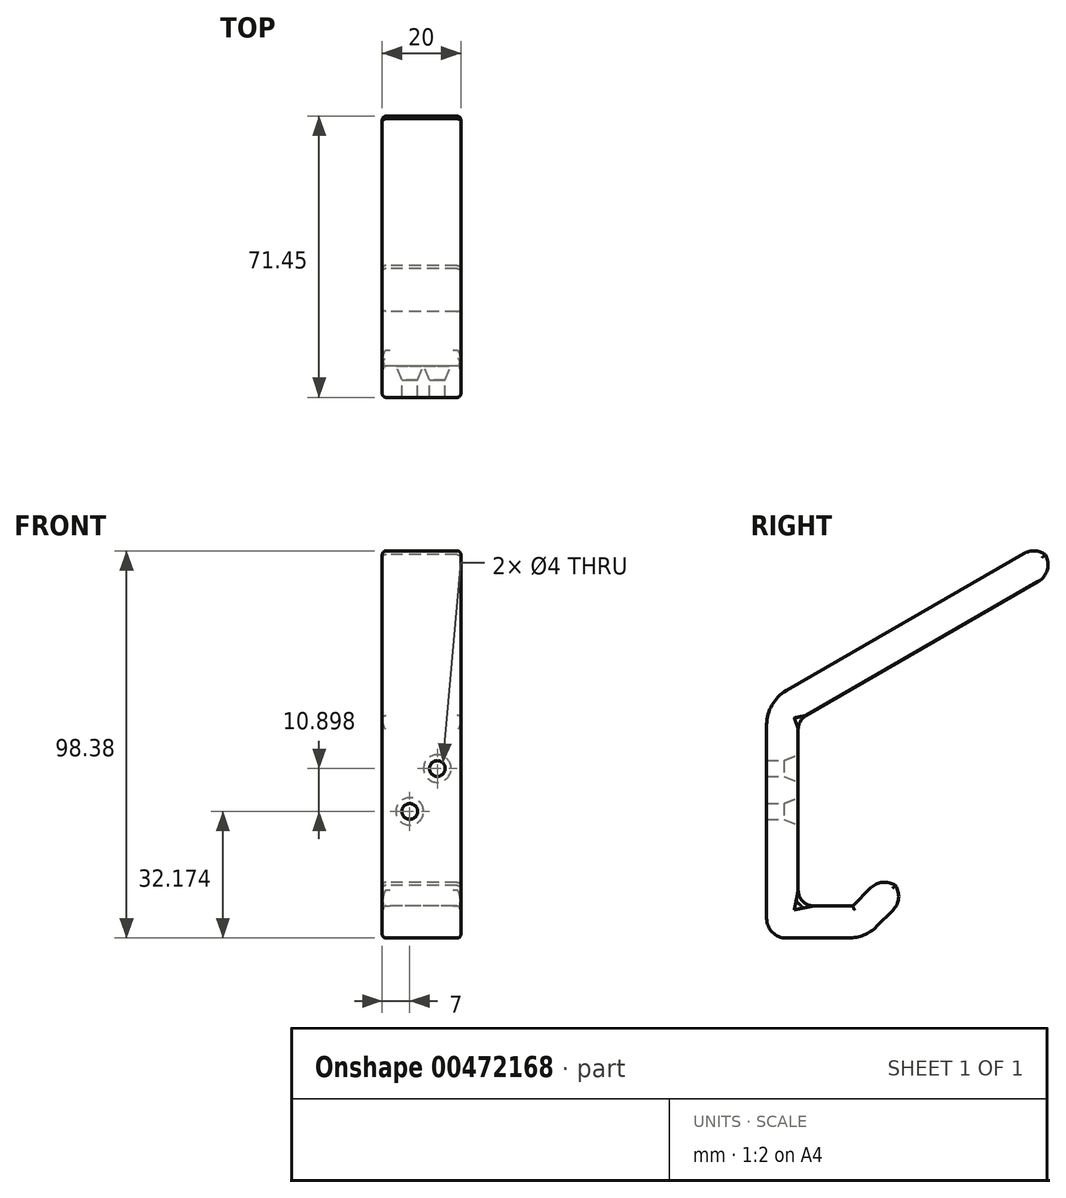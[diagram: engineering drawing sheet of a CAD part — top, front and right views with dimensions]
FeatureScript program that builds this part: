
annotation { "Feature Type Name" : "Feature", "Feature Type Description" : "" }
export const myFeature = defineFeature(function(context is Context, id is Id, definition is map)
    precondition{}
    {
        {
            var Q0;
            Q0=qCreatedBy(makeId("Right.planeOp"),FACE);
            var sketch = newSketch(context, id + "F0", { "sketchPlane" : qUnion([Q0])});
            skLineSegment(sketch, "E0", {"start": v(-17.53, 60) * mm, "end": v(51.75, 100) * mm});
            skLineSegment(sketch, "E1", {"start": v(7.47, 0) * mm, "end": v(18.07, 10.6) * mm});
            skLineSegment(sketch, "E2", {"start": v(51.75, 100) * mm, "end": v(55.75, 93.07) * mm});
            skLineSegment(sketch, "E3", {"start": v(55.75, 93.07) * mm, "end": v(-9.53, 55.38) * mm});
            skLineSegment(sketch, "E4", {"start": v(-9.53, 55.38) * mm, "end": v(-9.53, 8) * mm});
            skLineSegment(sketch, "E5", {"start": v(-9.71, 8.17) * mm, "end": v(4.33, 8.17) * mm});
            skLineSegment(sketch, "E6", {"start": v(18.07, 10.6) * mm, "end": v(12.42, 16.26) * mm});
            skLineSegment(sketch, "E7", {"start": v(12.42, 16.26) * mm, "end": v(4.33, 8.17) * mm});
            skLineSegment(sketch, "E8", {"start": v(-17.53, 60) * mm, "end": v(-17.53, 0) * mm});
            skLineSegment(sketch, "E9", {"start": v(7.47, 0) * mm, "end": v(-17.53, 0) * mm});
            skSolve(sketch);
        }
        {
            var Q0;
            Q0=makeQuery(id+"F0.imprint","IMPRINT",FACE,{"disambiguationData":[TD([[makeQuery(id+"F0.imprint","IMPRINT",EDGE,{"derivedFrom":sQuery(id+"F0.wireOp",EDGE,"E0")}),-1.0]])]});
            extrude(context, id + "F1", {"entities" : qUnion([Q0]), "depth" : 20 * mm});
        }
        {
            var Q0;
            Q0=makeQuery(id+"F1.opExtrude","SWEPT_EDGE",EDGE,{"disambiguationData":[OSD([sQuery(id+"F0.wireOp",EDGE,"E2"),sQuery(id+"F0.wireOp",EDGE,"E3")])]});
            fillet(context, id + "F2", {"entities" : qUnion([Q0]), "radius" : 5 * mm, "tangentPropagation" : true, "allowEdgeOverflow" : false});
        }
        {
            var Q0;
            Q0=makeQuery(id+"F1.opExtrude","SWEPT_EDGE",EDGE,{"disambiguationData":[OSD([sQuery(id+"F0.wireOp",EDGE,"E0"),sQuery(id+"F0.wireOp",EDGE,"E2")])]});
            fillet(context, id + "F3", {"entities" : qUnion([Q0]), "radius" : 5 * mm, "tangentPropagation" : true, "allowEdgeOverflow" : false});
        }
        {
            var Q0;
            Q0=makeQuery(id+"F1.opExtrude","SWEPT_EDGE",EDGE,{"disambiguationData":[OSD([sQuery(id+"F0.wireOp",EDGE,"E0"),sQuery(id+"F0.wireOp",EDGE,"E8")])]});
            fillet(context, id + "F4", {"entities" : qUnion([Q0]), "radius" : 10 * mm, "tangentPropagation" : true, "allowEdgeOverflow" : false});
        }
        {
            var Q0;
            Q0=makeQuery(id+"F1.opExtrude","SWEPT_EDGE",EDGE,{"disambiguationData":[OSD([sQuery(id+"F0.wireOp",EDGE,"E8"),sQuery(id+"F0.wireOp",EDGE,"E9")])]});
            fillet(context, id + "F5", {"entities" : qUnion([Q0]), "radius" : 5 * mm, "tangentPropagation" : true, "allowEdgeOverflow" : false});
        }
        {
            var Q0;
            Q0=makeQuery(id+"F1.opExtrude","SWEPT_EDGE",EDGE,{"disambiguationData":[OSD([sQuery(id+"F0.wireOp",EDGE,"E1"),sQuery(id+"F0.wireOp",EDGE,"E9")])]});
            fillet(context, id + "F6", {"entities" : qUnion([Q0]), "radius" : 10 * mm, "tangentPropagation" : true, "allowEdgeOverflow" : false});
        }
        {
            var Q0;
            Q0=makeQuery(id+"F1.opExtrude","SWEPT_EDGE",EDGE,{"disambiguationData":[OSD([sQuery(id+"F0.wireOp",EDGE,"E1"),sQuery(id+"F0.wireOp",EDGE,"E6")])]});
            var Q1;
            Q1=makeQuery(id+"F1.opExtrude","SWEPT_EDGE",EDGE,{"disambiguationData":[OSD([sQuery(id+"F0.wireOp",EDGE,"E6"),sQuery(id+"F0.wireOp",EDGE,"E7")])]});
            fillet(context, id + "F7", {"entities" : qUnion([Q0, Q1]), "radius" : 5 * mm, "tangentPropagation" : true, "allowEdgeOverflow" : false});
        }
        {
            var Q0;
            {var subQ0=sQuery(id+"F0.wireOp",EDGE,"E7");var subQ1=sQuery(id+"F0.wireOp",EDGE,"E6");Q0=makeQuery(id+"F7.opFillet","BLEND_EDGE",EDGE,{"blendedFrom":[makeQuery(id+"F1.opExtrude","SWEPT_EDGE",EDGE,{"disambiguationData":[OSD([subQ1,subQ0])]}),makeQuery(id+"F1.opExtrude","CAP_FACE",FACE,{"disambiguationData":[OSD([sQuery(id+"F0.wireOp",EDGE,"E0"),sQuery(id+"F0.wireOp",EDGE,"E1"),sQuery(id+"F0.wireOp",EDGE,"E2"),sQuery(id+"F0.wireOp",EDGE,"E3"),sQuery(id+"F0.wireOp",EDGE,"E4"),sQuery(id+"F0.wireOp",EDGE,"E5"),subQ1,subQ0,sQuery(id+"F0.wireOp",EDGE,"E8"),sQuery(id+"F0.wireOp",EDGE,"E9")])],"isStart":true})],"blendedInto":[makeQuery(id+"F1.opExtrude","CAP_FACE",FACE,{"disambiguationData":[OSD([sQuery(id+"F0.wireOp",EDGE,"E0"),sQuery(id+"F0.wireOp",EDGE,"E1"),sQuery(id+"F0.wireOp",EDGE,"E2"),sQuery(id+"F0.wireOp",EDGE,"E3"),sQuery(id+"F0.wireOp",EDGE,"E4"),sQuery(id+"F0.wireOp",EDGE,"E5"),subQ1,subQ0,sQuery(id+"F0.wireOp",EDGE,"E8"),sQuery(id+"F0.wireOp",EDGE,"E9")])],"isStart":true})]});}
            var Q1;
            {var subQ0=sQuery(id+"F0.wireOp",EDGE,"E6");var subQ1=sQuery(id+"F0.wireOp",EDGE,"E1");Q1=makeQuery(id+"F7.opFillet","BLEND_EDGE",EDGE,{"blendedFrom":[makeQuery(id+"F1.opExtrude","SWEPT_EDGE",EDGE,{"disambiguationData":[OSD([subQ1,subQ0])]}),makeQuery(id+"F1.opExtrude","CAP_FACE",FACE,{"disambiguationData":[OSD([sQuery(id+"F0.wireOp",EDGE,"E0"),subQ1,sQuery(id+"F0.wireOp",EDGE,"E2"),sQuery(id+"F0.wireOp",EDGE,"E3"),sQuery(id+"F0.wireOp",EDGE,"E4"),sQuery(id+"F0.wireOp",EDGE,"E5"),subQ0,sQuery(id+"F0.wireOp",EDGE,"E7"),sQuery(id+"F0.wireOp",EDGE,"E8"),sQuery(id+"F0.wireOp",EDGE,"E9")])],"isStart":true})],"blendedInto":[makeQuery(id+"F1.opExtrude","CAP_FACE",FACE,{"disambiguationData":[OSD([sQuery(id+"F0.wireOp",EDGE,"E0"),subQ1,sQuery(id+"F0.wireOp",EDGE,"E2"),sQuery(id+"F0.wireOp",EDGE,"E3"),sQuery(id+"F0.wireOp",EDGE,"E4"),sQuery(id+"F0.wireOp",EDGE,"E5"),subQ0,sQuery(id+"F0.wireOp",EDGE,"E7"),sQuery(id+"F0.wireOp",EDGE,"E8"),sQuery(id+"F0.wireOp",EDGE,"E9")])],"isStart":true})]});}
            var Q2;
            Q2=makeQuery(id+"F1.opExtrude","CAP_EDGE",EDGE,{"disambiguationData":[OSD([sQuery(id+"F0.wireOp",EDGE,"E7")])],"isStart":true});
            var Q3;
            Q3=makeQuery(id+"F1.opExtrude","CAP_EDGE",EDGE,{"disambiguationData":[OSD([sQuery(id+"F0.wireOp",EDGE,"E5")])],"isStart":true});
            var Q4;
            {var subQ0=sQuery(id+"F0.wireOp",EDGE,"E9");var subQ1=sQuery(id+"F0.wireOp",EDGE,"E1");Q4=makeQuery(id+"F6.opFillet","BLEND_EDGE",EDGE,{"blendedFrom":[makeQuery(id+"F1.opExtrude","SWEPT_EDGE",EDGE,{"disambiguationData":[OSD([subQ1,subQ0])]}),makeQuery(id+"F1.opExtrude","CAP_FACE",FACE,{"disambiguationData":[OSD([sQuery(id+"F0.wireOp",EDGE,"E0"),subQ1,sQuery(id+"F0.wireOp",EDGE,"E2"),sQuery(id+"F0.wireOp",EDGE,"E3"),sQuery(id+"F0.wireOp",EDGE,"E4"),sQuery(id+"F0.wireOp",EDGE,"E5"),sQuery(id+"F0.wireOp",EDGE,"E6"),sQuery(id+"F0.wireOp",EDGE,"E7"),sQuery(id+"F0.wireOp",EDGE,"E8"),subQ0])],"isStart":true})],"blendedInto":[makeQuery(id+"F1.opExtrude","CAP_FACE",FACE,{"disambiguationData":[OSD([sQuery(id+"F0.wireOp",EDGE,"E0"),subQ1,sQuery(id+"F0.wireOp",EDGE,"E2"),sQuery(id+"F0.wireOp",EDGE,"E3"),sQuery(id+"F0.wireOp",EDGE,"E4"),sQuery(id+"F0.wireOp",EDGE,"E5"),sQuery(id+"F0.wireOp",EDGE,"E6"),sQuery(id+"F0.wireOp",EDGE,"E7"),sQuery(id+"F0.wireOp",EDGE,"E8"),subQ0])],"isStart":true})]});}
            var Q5;
            Q5=makeQuery(id+"F1.opExtrude","CAP_EDGE",EDGE,{"disambiguationData":[OSD([sQuery(id+"F0.wireOp",EDGE,"E1")])],"isStart":true});
            var Q6;
            Q6=makeQuery(id+"F1.opExtrude","CAP_EDGE",EDGE,{"disambiguationData":[OSD([sQuery(id+"F0.wireOp",EDGE,"E9")])],"isStart":true});
            var Q7;
            {var subQ0=sQuery(id+"F0.wireOp",EDGE,"E9");var subQ1=sQuery(id+"F0.wireOp",EDGE,"E8");Q7=makeQuery(id+"F5.opFillet","BLEND_EDGE",EDGE,{"blendedFrom":[makeQuery(id+"F1.opExtrude","SWEPT_EDGE",EDGE,{"disambiguationData":[OSD([subQ1,subQ0])]}),makeQuery(id+"F1.opExtrude","CAP_FACE",FACE,{"disambiguationData":[OSD([sQuery(id+"F0.wireOp",EDGE,"E0"),sQuery(id+"F0.wireOp",EDGE,"E1"),sQuery(id+"F0.wireOp",EDGE,"E2"),sQuery(id+"F0.wireOp",EDGE,"E3"),sQuery(id+"F0.wireOp",EDGE,"E4"),sQuery(id+"F0.wireOp",EDGE,"E5"),sQuery(id+"F0.wireOp",EDGE,"E6"),sQuery(id+"F0.wireOp",EDGE,"E7"),subQ1,subQ0])],"isStart":true})],"blendedInto":[makeQuery(id+"F1.opExtrude","CAP_FACE",FACE,{"disambiguationData":[OSD([sQuery(id+"F0.wireOp",EDGE,"E0"),sQuery(id+"F0.wireOp",EDGE,"E1"),sQuery(id+"F0.wireOp",EDGE,"E2"),sQuery(id+"F0.wireOp",EDGE,"E3"),sQuery(id+"F0.wireOp",EDGE,"E4"),sQuery(id+"F0.wireOp",EDGE,"E5"),sQuery(id+"F0.wireOp",EDGE,"E6"),sQuery(id+"F0.wireOp",EDGE,"E7"),subQ1,subQ0])],"isStart":true})]});}
            var Q8;
            Q8=makeQuery(id+"F1.opExtrude","CAP_EDGE",EDGE,{"disambiguationData":[OSD([sQuery(id+"F0.wireOp",EDGE,"E8")])],"isStart":true});
            var Q9;
            Q9=makeQuery(id+"F1.opExtrude","CAP_EDGE",EDGE,{"disambiguationData":[OSD([sQuery(id+"F0.wireOp",EDGE,"E4")])],"isStart":true});
            var Q10;
            Q10=makeQuery(id+"F1.opExtrude","CAP_EDGE",EDGE,{"disambiguationData":[OSD([sQuery(id+"F0.wireOp",EDGE,"E3")])],"isStart":true});
            var Q11;
            Q11=makeQuery(id+"F1.opExtrude","CAP_EDGE",EDGE,{"disambiguationData":[OSD([sQuery(id+"F0.wireOp",EDGE,"E0")])],"isStart":true});
            var Q12;
            {var subQ0=sQuery(id+"F0.wireOp",EDGE,"E2");var subQ1=sQuery(id+"F0.wireOp",EDGE,"E0");Q12=makeQuery(id+"F3.opFillet","BLEND_EDGE",EDGE,{"blendedFrom":[makeQuery(id+"F1.opExtrude","SWEPT_EDGE",EDGE,{"disambiguationData":[OSD([subQ1,subQ0])]}),makeQuery(id+"F1.opExtrude","CAP_FACE",FACE,{"disambiguationData":[OSD([subQ1,sQuery(id+"F0.wireOp",EDGE,"E1"),subQ0,sQuery(id+"F0.wireOp",EDGE,"E3"),sQuery(id+"F0.wireOp",EDGE,"E4"),sQuery(id+"F0.wireOp",EDGE,"E5"),sQuery(id+"F0.wireOp",EDGE,"E6"),sQuery(id+"F0.wireOp",EDGE,"E7"),sQuery(id+"F0.wireOp",EDGE,"E8"),sQuery(id+"F0.wireOp",EDGE,"E9")])],"isStart":true})],"blendedInto":[makeQuery(id+"F1.opExtrude","CAP_FACE",FACE,{"disambiguationData":[OSD([subQ1,sQuery(id+"F0.wireOp",EDGE,"E1"),subQ0,sQuery(id+"F0.wireOp",EDGE,"E3"),sQuery(id+"F0.wireOp",EDGE,"E4"),sQuery(id+"F0.wireOp",EDGE,"E5"),sQuery(id+"F0.wireOp",EDGE,"E6"),sQuery(id+"F0.wireOp",EDGE,"E7"),sQuery(id+"F0.wireOp",EDGE,"E8"),sQuery(id+"F0.wireOp",EDGE,"E9")])],"isStart":true})]});}
            var Q13;
            {var subQ0=sQuery(id+"F0.wireOp",EDGE,"E3");var subQ1=sQuery(id+"F0.wireOp",EDGE,"E2");Q13=makeQuery(id+"F2.opFillet","BLEND_EDGE",EDGE,{"blendedFrom":[makeQuery(id+"F1.opExtrude","SWEPT_EDGE",EDGE,{"disambiguationData":[OSD([subQ1,subQ0])]}),makeQuery(id+"F1.opExtrude","CAP_FACE",FACE,{"disambiguationData":[OSD([sQuery(id+"F0.wireOp",EDGE,"E0"),sQuery(id+"F0.wireOp",EDGE,"E1"),subQ1,subQ0,sQuery(id+"F0.wireOp",EDGE,"E4"),sQuery(id+"F0.wireOp",EDGE,"E5"),sQuery(id+"F0.wireOp",EDGE,"E6"),sQuery(id+"F0.wireOp",EDGE,"E7"),sQuery(id+"F0.wireOp",EDGE,"E8"),sQuery(id+"F0.wireOp",EDGE,"E9")])],"isStart":true})],"blendedInto":[makeQuery(id+"F1.opExtrude","CAP_FACE",FACE,{"disambiguationData":[OSD([sQuery(id+"F0.wireOp",EDGE,"E0"),sQuery(id+"F0.wireOp",EDGE,"E1"),subQ1,subQ0,sQuery(id+"F0.wireOp",EDGE,"E4"),sQuery(id+"F0.wireOp",EDGE,"E5"),sQuery(id+"F0.wireOp",EDGE,"E6"),sQuery(id+"F0.wireOp",EDGE,"E7"),sQuery(id+"F0.wireOp",EDGE,"E8"),sQuery(id+"F0.wireOp",EDGE,"E9")])],"isStart":true})]});}
            var Q14;
            {var subQ0=sQuery(id+"F0.wireOp",EDGE,"E8");var subQ1=sQuery(id+"F0.wireOp",EDGE,"E0");Q14=makeQuery(id+"F4.opFillet","BLEND_EDGE",EDGE,{"blendedFrom":[makeQuery(id+"F1.opExtrude","SWEPT_EDGE",EDGE,{"disambiguationData":[OSD([subQ1,subQ0])]}),makeQuery(id+"F1.opExtrude","CAP_FACE",FACE,{"disambiguationData":[OSD([subQ1,sQuery(id+"F0.wireOp",EDGE,"E1"),sQuery(id+"F0.wireOp",EDGE,"E2"),sQuery(id+"F0.wireOp",EDGE,"E3"),sQuery(id+"F0.wireOp",EDGE,"E4"),sQuery(id+"F0.wireOp",EDGE,"E5"),sQuery(id+"F0.wireOp",EDGE,"E6"),sQuery(id+"F0.wireOp",EDGE,"E7"),subQ0,sQuery(id+"F0.wireOp",EDGE,"E9")])],"isStart":true})],"blendedInto":[makeQuery(id+"F1.opExtrude","CAP_FACE",FACE,{"disambiguationData":[OSD([subQ1,sQuery(id+"F0.wireOp",EDGE,"E1"),sQuery(id+"F0.wireOp",EDGE,"E2"),sQuery(id+"F0.wireOp",EDGE,"E3"),sQuery(id+"F0.wireOp",EDGE,"E4"),sQuery(id+"F0.wireOp",EDGE,"E5"),sQuery(id+"F0.wireOp",EDGE,"E6"),sQuery(id+"F0.wireOp",EDGE,"E7"),subQ0,sQuery(id+"F0.wireOp",EDGE,"E9")])],"isStart":true})]});}
            var Q15;
            Q15=makeQuery(id+"F1.opExtrude","CAP_EDGE",EDGE,{"disambiguationData":[OSD([sQuery(id+"F0.wireOp",EDGE,"E0")])],"isStart":false});
            var Q16;
            Q16=makeQuery(id+"F1.opExtrude","CAP_EDGE",EDGE,{"disambiguationData":[OSD([sQuery(id+"F0.wireOp",EDGE,"E3")])],"isStart":false});
            var Q17;
            {var subQ0=sQuery(id+"F0.wireOp",EDGE,"E8");var subQ1=sQuery(id+"F0.wireOp",EDGE,"E0");Q17=makeQuery(id+"F4.opFillet","BLEND_EDGE",EDGE,{"blendedFrom":[makeQuery(id+"F1.opExtrude","SWEPT_EDGE",EDGE,{"disambiguationData":[OSD([subQ1,subQ0])]}),makeQuery(id+"F1.opExtrude","CAP_FACE",FACE,{"disambiguationData":[OSD([subQ1,sQuery(id+"F0.wireOp",EDGE,"E1"),sQuery(id+"F0.wireOp",EDGE,"E2"),sQuery(id+"F0.wireOp",EDGE,"E3"),sQuery(id+"F0.wireOp",EDGE,"E4"),sQuery(id+"F0.wireOp",EDGE,"E5"),sQuery(id+"F0.wireOp",EDGE,"E6"),sQuery(id+"F0.wireOp",EDGE,"E7"),subQ0,sQuery(id+"F0.wireOp",EDGE,"E9")])],"isStart":false})],"blendedInto":[makeQuery(id+"F1.opExtrude","CAP_FACE",FACE,{"disambiguationData":[OSD([subQ1,sQuery(id+"F0.wireOp",EDGE,"E1"),sQuery(id+"F0.wireOp",EDGE,"E2"),sQuery(id+"F0.wireOp",EDGE,"E3"),sQuery(id+"F0.wireOp",EDGE,"E4"),sQuery(id+"F0.wireOp",EDGE,"E5"),sQuery(id+"F0.wireOp",EDGE,"E6"),sQuery(id+"F0.wireOp",EDGE,"E7"),subQ0,sQuery(id+"F0.wireOp",EDGE,"E9")])],"isStart":false})]});}
            var Q18;
            {var subQ0=sQuery(id+"F0.wireOp",EDGE,"E2");var subQ1=sQuery(id+"F0.wireOp",EDGE,"E0");Q18=makeQuery(id+"F3.opFillet","BLEND_EDGE",EDGE,{"blendedFrom":[makeQuery(id+"F1.opExtrude","SWEPT_EDGE",EDGE,{"disambiguationData":[OSD([subQ1,subQ0])]}),makeQuery(id+"F1.opExtrude","CAP_FACE",FACE,{"disambiguationData":[OSD([subQ1,sQuery(id+"F0.wireOp",EDGE,"E1"),subQ0,sQuery(id+"F0.wireOp",EDGE,"E3"),sQuery(id+"F0.wireOp",EDGE,"E4"),sQuery(id+"F0.wireOp",EDGE,"E5"),sQuery(id+"F0.wireOp",EDGE,"E6"),sQuery(id+"F0.wireOp",EDGE,"E7"),sQuery(id+"F0.wireOp",EDGE,"E8"),sQuery(id+"F0.wireOp",EDGE,"E9")])],"isStart":false})],"blendedInto":[makeQuery(id+"F1.opExtrude","CAP_FACE",FACE,{"disambiguationData":[OSD([subQ1,sQuery(id+"F0.wireOp",EDGE,"E1"),subQ0,sQuery(id+"F0.wireOp",EDGE,"E3"),sQuery(id+"F0.wireOp",EDGE,"E4"),sQuery(id+"F0.wireOp",EDGE,"E5"),sQuery(id+"F0.wireOp",EDGE,"E6"),sQuery(id+"F0.wireOp",EDGE,"E7"),sQuery(id+"F0.wireOp",EDGE,"E8"),sQuery(id+"F0.wireOp",EDGE,"E9")])],"isStart":false})]});}
            var Q19;
            {var subQ0=sQuery(id+"F0.wireOp",EDGE,"E3");var subQ1=sQuery(id+"F0.wireOp",EDGE,"E2");Q19=makeQuery(id+"F2.opFillet","BLEND_EDGE",EDGE,{"blendedFrom":[makeQuery(id+"F1.opExtrude","SWEPT_EDGE",EDGE,{"disambiguationData":[OSD([subQ1,subQ0])]}),makeQuery(id+"F1.opExtrude","CAP_FACE",FACE,{"disambiguationData":[OSD([sQuery(id+"F0.wireOp",EDGE,"E0"),sQuery(id+"F0.wireOp",EDGE,"E1"),subQ1,subQ0,sQuery(id+"F0.wireOp",EDGE,"E4"),sQuery(id+"F0.wireOp",EDGE,"E5"),sQuery(id+"F0.wireOp",EDGE,"E6"),sQuery(id+"F0.wireOp",EDGE,"E7"),sQuery(id+"F0.wireOp",EDGE,"E8"),sQuery(id+"F0.wireOp",EDGE,"E9")])],"isStart":false})],"blendedInto":[makeQuery(id+"F1.opExtrude","CAP_FACE",FACE,{"disambiguationData":[OSD([sQuery(id+"F0.wireOp",EDGE,"E0"),sQuery(id+"F0.wireOp",EDGE,"E1"),subQ1,subQ0,sQuery(id+"F0.wireOp",EDGE,"E4"),sQuery(id+"F0.wireOp",EDGE,"E5"),sQuery(id+"F0.wireOp",EDGE,"E6"),sQuery(id+"F0.wireOp",EDGE,"E7"),sQuery(id+"F0.wireOp",EDGE,"E8"),sQuery(id+"F0.wireOp",EDGE,"E9")])],"isStart":false})]});}
            var Q20;
            Q20=makeQuery(id+"F1.opExtrude","CAP_EDGE",EDGE,{"disambiguationData":[OSD([sQuery(id+"F0.wireOp",EDGE,"E4")])],"isStart":false});
            var Q21;
            Q21=makeQuery(id+"F1.opExtrude","CAP_EDGE",EDGE,{"disambiguationData":[OSD([sQuery(id+"F0.wireOp",EDGE,"E8")])],"isStart":false});
            var Q22;
            {var subQ0=sQuery(id+"F0.wireOp",EDGE,"E9");var subQ1=sQuery(id+"F0.wireOp",EDGE,"E8");Q22=makeQuery(id+"F5.opFillet","BLEND_EDGE",EDGE,{"blendedFrom":[makeQuery(id+"F1.opExtrude","SWEPT_EDGE",EDGE,{"disambiguationData":[OSD([subQ1,subQ0])]}),makeQuery(id+"F1.opExtrude","CAP_FACE",FACE,{"disambiguationData":[OSD([sQuery(id+"F0.wireOp",EDGE,"E0"),sQuery(id+"F0.wireOp",EDGE,"E1"),sQuery(id+"F0.wireOp",EDGE,"E2"),sQuery(id+"F0.wireOp",EDGE,"E3"),sQuery(id+"F0.wireOp",EDGE,"E4"),sQuery(id+"F0.wireOp",EDGE,"E5"),sQuery(id+"F0.wireOp",EDGE,"E6"),sQuery(id+"F0.wireOp",EDGE,"E7"),subQ1,subQ0])],"isStart":false})],"blendedInto":[makeQuery(id+"F1.opExtrude","CAP_FACE",FACE,{"disambiguationData":[OSD([sQuery(id+"F0.wireOp",EDGE,"E0"),sQuery(id+"F0.wireOp",EDGE,"E1"),sQuery(id+"F0.wireOp",EDGE,"E2"),sQuery(id+"F0.wireOp",EDGE,"E3"),sQuery(id+"F0.wireOp",EDGE,"E4"),sQuery(id+"F0.wireOp",EDGE,"E5"),sQuery(id+"F0.wireOp",EDGE,"E6"),sQuery(id+"F0.wireOp",EDGE,"E7"),subQ1,subQ0])],"isStart":false})]});}
            var Q23;
            Q23=makeQuery(id+"F1.opExtrude","CAP_EDGE",EDGE,{"disambiguationData":[OSD([sQuery(id+"F0.wireOp",EDGE,"E9")])],"isStart":false});
            var Q24;
            Q24=makeQuery(id+"F1.opExtrude","CAP_EDGE",EDGE,{"disambiguationData":[OSD([sQuery(id+"F0.wireOp",EDGE,"E5")])],"isStart":false});
            var Q25;
            Q25=makeQuery(id+"F1.opExtrude","CAP_EDGE",EDGE,{"disambiguationData":[OSD([sQuery(id+"F0.wireOp",EDGE,"E7")])],"isStart":false});
            var Q26;
            {var subQ0=sQuery(id+"F0.wireOp",EDGE,"E7");var subQ1=sQuery(id+"F0.wireOp",EDGE,"E6");Q26=makeQuery(id+"F7.opFillet","BLEND_EDGE",EDGE,{"blendedFrom":[makeQuery(id+"F1.opExtrude","SWEPT_EDGE",EDGE,{"disambiguationData":[OSD([subQ1,subQ0])]}),makeQuery(id+"F1.opExtrude","CAP_FACE",FACE,{"disambiguationData":[OSD([sQuery(id+"F0.wireOp",EDGE,"E0"),sQuery(id+"F0.wireOp",EDGE,"E1"),sQuery(id+"F0.wireOp",EDGE,"E2"),sQuery(id+"F0.wireOp",EDGE,"E3"),sQuery(id+"F0.wireOp",EDGE,"E4"),sQuery(id+"F0.wireOp",EDGE,"E5"),subQ1,subQ0,sQuery(id+"F0.wireOp",EDGE,"E8"),sQuery(id+"F0.wireOp",EDGE,"E9")])],"isStart":false})],"blendedInto":[makeQuery(id+"F1.opExtrude","CAP_FACE",FACE,{"disambiguationData":[OSD([sQuery(id+"F0.wireOp",EDGE,"E0"),sQuery(id+"F0.wireOp",EDGE,"E1"),sQuery(id+"F0.wireOp",EDGE,"E2"),sQuery(id+"F0.wireOp",EDGE,"E3"),sQuery(id+"F0.wireOp",EDGE,"E4"),sQuery(id+"F0.wireOp",EDGE,"E5"),subQ1,subQ0,sQuery(id+"F0.wireOp",EDGE,"E8"),sQuery(id+"F0.wireOp",EDGE,"E9")])],"isStart":false})]});}
            var Q27;
            {var subQ0=sQuery(id+"F0.wireOp",EDGE,"E9");var subQ1=sQuery(id+"F0.wireOp",EDGE,"E1");Q27=makeQuery(id+"F6.opFillet","BLEND_EDGE",EDGE,{"blendedFrom":[makeQuery(id+"F1.opExtrude","SWEPT_EDGE",EDGE,{"disambiguationData":[OSD([subQ1,subQ0])]}),makeQuery(id+"F1.opExtrude","CAP_FACE",FACE,{"disambiguationData":[OSD([sQuery(id+"F0.wireOp",EDGE,"E0"),subQ1,sQuery(id+"F0.wireOp",EDGE,"E2"),sQuery(id+"F0.wireOp",EDGE,"E3"),sQuery(id+"F0.wireOp",EDGE,"E4"),sQuery(id+"F0.wireOp",EDGE,"E5"),sQuery(id+"F0.wireOp",EDGE,"E6"),sQuery(id+"F0.wireOp",EDGE,"E7"),sQuery(id+"F0.wireOp",EDGE,"E8"),subQ0])],"isStart":false})],"blendedInto":[makeQuery(id+"F1.opExtrude","CAP_FACE",FACE,{"disambiguationData":[OSD([sQuery(id+"F0.wireOp",EDGE,"E0"),subQ1,sQuery(id+"F0.wireOp",EDGE,"E2"),sQuery(id+"F0.wireOp",EDGE,"E3"),sQuery(id+"F0.wireOp",EDGE,"E4"),sQuery(id+"F0.wireOp",EDGE,"E5"),sQuery(id+"F0.wireOp",EDGE,"E6"),sQuery(id+"F0.wireOp",EDGE,"E7"),sQuery(id+"F0.wireOp",EDGE,"E8"),subQ0])],"isStart":false})]});}
            var Q28;
            {var subQ0=sQuery(id+"F0.wireOp",EDGE,"E6");var subQ1=sQuery(id+"F0.wireOp",EDGE,"E1");Q28=makeQuery(id+"F7.opFillet","BLEND_EDGE",EDGE,{"blendedFrom":[makeQuery(id+"F1.opExtrude","SWEPT_EDGE",EDGE,{"disambiguationData":[OSD([subQ1,subQ0])]}),makeQuery(id+"F1.opExtrude","CAP_FACE",FACE,{"disambiguationData":[OSD([sQuery(id+"F0.wireOp",EDGE,"E0"),subQ1,sQuery(id+"F0.wireOp",EDGE,"E2"),sQuery(id+"F0.wireOp",EDGE,"E3"),sQuery(id+"F0.wireOp",EDGE,"E4"),sQuery(id+"F0.wireOp",EDGE,"E5"),subQ0,sQuery(id+"F0.wireOp",EDGE,"E7"),sQuery(id+"F0.wireOp",EDGE,"E8"),sQuery(id+"F0.wireOp",EDGE,"E9")])],"isStart":false})],"blendedInto":[makeQuery(id+"F1.opExtrude","CAP_FACE",FACE,{"disambiguationData":[OSD([sQuery(id+"F0.wireOp",EDGE,"E0"),subQ1,sQuery(id+"F0.wireOp",EDGE,"E2"),sQuery(id+"F0.wireOp",EDGE,"E3"),sQuery(id+"F0.wireOp",EDGE,"E4"),sQuery(id+"F0.wireOp",EDGE,"E5"),subQ0,sQuery(id+"F0.wireOp",EDGE,"E7"),sQuery(id+"F0.wireOp",EDGE,"E8"),sQuery(id+"F0.wireOp",EDGE,"E9")])],"isStart":false})]});}
            var Q29;
            Q29=makeQuery(id+"F1.opExtrude","CAP_EDGE",EDGE,{"disambiguationData":[OSD([sQuery(id+"F0.wireOp",EDGE,"E1")])],"isStart":false});
            fillet(context, id + "F8", {"entities" : qUnion([Q0, Q1, Q2, Q3, Q4, Q5, Q6, Q7, Q8, Q9, Q10, Q11, Q12, Q13, Q14, Q15, Q16, Q17, Q18, Q19, Q20, Q21, Q22, Q23, Q24, Q25, Q26, Q27, Q28, Q29]), "radius" : 1 * mm, "tangentPropagation" : true, "allowEdgeOverflow" : false});
        }
        {
            var Q0;
            Q0=makeQuery(id+"F1.opExtrude","SWEPT_EDGE",EDGE,{"disambiguationData":[OSD([sQuery(id+"F0.wireOp",EDGE,"E4"),sQuery(id+"F0.wireOp",EDGE,"E5")])]});
            var Q1;
            Q1=makeQuery(id+"F1.opExtrude","SWEPT_EDGE",EDGE,{"disambiguationData":[OSD([sQuery(id+"F0.wireOp",EDGE,"E3"),sQuery(id+"F0.wireOp",EDGE,"E4")])]});
            fillet(context, id + "F9", {"entities" : qUnion([Q0, Q1]), "radius" : 4 * mm, "tangentPropagation" : true, "allowEdgeOverflow" : false});
        }
        {
            var Q0;
            Q0=makeQuery(id+"F1.opExtrude","SWEPT_FACE",FACE,{"disambiguationData":[OSD([sQuery(id+"F0.wireOp",EDGE,"E4")])]});
            var sketch = newSketch(context, id + "F10", { "sketchPlane" : qUnion([Q0])});
            skPoint(sketch, "E10", {"position": v(-14, 43.07) * mm});
            skPoint(sketch, "E11", {"position": v(-7, 32.17) * mm});
            skSolve(sketch);
        }
        {
            var Q0;
            Q0=sQuery(id+"F10.wireOp",VERTEX,"E10");
            var Q1;
            Q1=sQuery(id+"F10.wireOp",VERTEX,"E11");
            var Q2;
            Q2=makeQuery(id+"F1.opExtrude","SWEPT_BODY",BODY,{"disambiguationData":[OSD([sQuery(id+"F0.wireOp",EDGE,"E0"),sQuery(id+"F0.wireOp",EDGE,"E1"),sQuery(id+"F0.wireOp",EDGE,"E2"),sQuery(id+"F0.wireOp",EDGE,"E3"),sQuery(id+"F0.wireOp",EDGE,"E4"),sQuery(id+"F0.wireOp",EDGE,"E5"),sQuery(id+"F0.wireOp",EDGE,"E6"),sQuery(id+"F0.wireOp",EDGE,"E7"),sQuery(id+"F0.wireOp",EDGE,"E8"),sQuery(id+"F0.wireOp",EDGE,"E9")])]});
            hole(context, id + "F11", {"style" : HoleStyle.C_SINK, "endStyle" : HoleEndStyle.THROUGH, "holeDiameter" : 4 * mm, "cSinkDiameter" : 7 * mm, "cSinkAngle" : 45 * degree, "isTappedThrough" : true, "tappedDepth" : 12 * mm, "tapClearance" : 3, "startFromSketch" : true, "locations" : qUnion([Q0, Q1]), "scope" : qUnion([Q2])});
        }
    });
